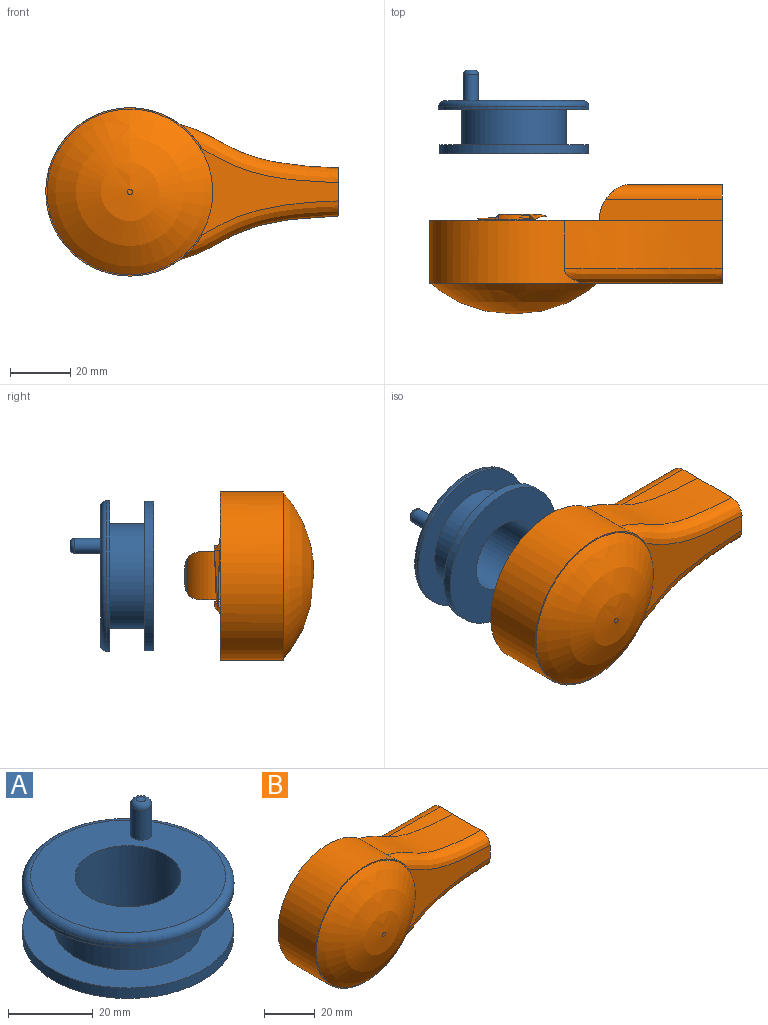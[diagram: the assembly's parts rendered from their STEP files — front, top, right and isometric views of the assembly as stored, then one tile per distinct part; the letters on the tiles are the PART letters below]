
ASSEMBLY  parts=2 mates=1
PART A: 12 faces, bbox 54.1x54.1x27.8 mm
  f0: cylinder r=24.83mm len=49.66mm, axis (0,0,1), area 468.1mm2, adj f1,f6
  f1: plane 49.66x49.66mm, normal (0,0,-1), area 1446.3mm2, adj f0,f8
  f2: plane 46x46mm, normal (0,0,1), area 1151.4mm2, adj f7,f8,f9
  f3: cylinder r=25mm len=50mm, axis (0,0,1), area 157.1mm2, adj f4,f7
  f4: plane 50x50mm, normal (0,0,-1), area 1013.2mm2, adj f3,f5
  f5: cylinder r=17.39mm len=34.78mm, axis (0,0,1), area 1280.1mm2, adj f4,f6
  f6: plane 49.66x49.66mm, normal (0,0,1), area 986.9mm2, adj f0,f5
  f7: torus R=23mm, axis (0,0,1), area 479.1mm2, adj f2,f3
  f8: cylinder r=12.5mm len=25mm, axis (0,0,-1), area 1391.3mm2, adj f1,f2
  f9: cylinder r=2.5mm len=8.65mm, axis (0,0,-1), area 135.9mm2, adj f2,f11
  f10: plane 2.1x2.1mm, normal (0,0,1), area 3.5mm2, adj f11
  f11: torus R=1.05mm, axis (0,0,1), area 28.2mm2, adj f9,f10
PART B: 48 faces, bbox 98.5x43.1x56.2 mm
  f0: plane 31.66x5.98mm, normal (0,1,0), area 189.4mm2, adj f5,f45,f46,f47
  f1: plane 40.96x7mm, normal (0,0,1), area 282mm2, adj f3,f5,f44,f46
  f2: plane 40.96x7mm, normal (0,0,-1), area 282mm2, adj f3,f5,f44,f45
  f3: plane 52.61x44.99mm, normal (0,1,0), area 351.1mm2, adj f1,f2,f6,f8,f9,f44
  f4: plane 97.29x56mm, normal (0,-1,0), area 572.5mm2, adj f5,f6,f10,f11,f16
  f5: plane 32.98x16.16mm, normal (1,0,0), area 393.7mm2, adj f0,f1,f2,f4,f8,f9,f10,f11
  f6: cylinder r=28mm len=56mm, axis (0,-1,0), area 2663.9mm2, adj f3,f4,f7,f8,f9,f10,f11
  f7: plane 56x56mm, normal (0,1,0), area 251.5mm2, adj f6,f17
  f8: extruded ~52.61x15.8mm, area 873.4mm2, adj f3,f5,f6,f11
  f9: extruded ~52.61x15.8mm, area 873.4mm2, adj f3,f5,f6,f10
  f10: bspline ~56.16x19.87mm, area 399.3mm2, adj f4,f5,f6,f9
  f11: bspline ~56.16x19.87mm, area 399.3mm2, adj f4,f5,f6,f8
  f12: cylinder r=1.97mm len=38.53mm, axis (1,0,0), area 472.9mm2, adj f5,f43
  f13: cylinder r=5.55mm len=22mm, axis (1,0,0), area 767.2mm2, adj f5,f14
  f14: plane 11.1x11.1mm, normal (1,0,0), area 96.8mm2, adj f13
  f15: plane 1.77x1.77mm, normal (0,-1,0), area 2.4mm2, adj f16
  f16: torus R=0.88mm, axis (0,1,0), area 2720.3mm2, adj f4,f15
  f17: cylinder r=26.53mm len=53.06mm, axis (0,1,0), area 2871.9mm2, adj f7,f42,f43
  f18: revolved ~13.13x4.04mm, area 38.8mm2, adj f19,f26,f27,f28
  f19: bspline ~14.86x2.84mm, area 3.5mm2, adj f18,f20,f26,f28
  f20: plane 13.07x2.36mm, normal (0,-1,0), area 5.8mm2, adj f19,f26,f28,f29
  f21: revolved ~13.13x4.04mm, area 38.8mm2, adj f22,f30,f31,f32
  f22: bspline ~14.86x2.84mm, area 3.5mm2, adj f21,f23,f30,f32
  f23: plane 13.07x2.36mm, normal (0,-1,0), area 5.8mm2, adj f22,f30,f32,f33
  f24: plane 17.81x5.18mm, normal (0,1,0), area 37.1mm2, adj f34,f35,f36,f37
  f25: plane 17.81x5.18mm, normal (0,1,0), area 37.1mm2, adj f38,f39,f40,f41
  f26: plane 20.02x2.06mm, normal (0.79,0,-0.61), area 39.8mm2, adj f18,f19,f20,f27,f29,f42
  f27: cylinder r=10.03mm len=20mm, axis (0,-1,0), area 220.7mm2, adj f18,f26,f28,f42
  f28: plane 20.02x2.36mm, normal (-0.91,0,-0.42), area 39.8mm2, adj f18,f19,f20,f27,f29,f42
  f29: cylinder r=12.08mm len=18mm, axis (0,-1,0), area 239.1mm2, adj f20,f26,f28,f42
  f30: plane 20.02x2.06mm, normal (-0.79,0,0.61), area 39.8mm2, adj f21,f22,f23,f31,f33,f42
  f31: cylinder r=10.03mm len=20mm, axis (0,-1,0), area 220.7mm2, adj f21,f30,f32,f42
  f32: plane 20.02x2.36mm, normal (0.91,0,0.42), area 39.8mm2, adj f21,f22,f23,f31,f33,f42
  f33: cylinder r=12.08mm len=18mm, axis (0,-1,0), area 239.1mm2, adj f23,f30,f32,f42
  f34: plane 18x1.62mm, normal (0.79,0,0.61), area 37mm2, adj f24,f35,f37,f42
  f35: cylinder r=10.03mm len=18mm, axis (0,-1,0), area 293.5mm2, adj f24,f34,f36,f42
  f36: plane 18x1.62mm, normal (0.79,0,-0.61), area 37mm2, adj f24,f35,f37,f42
  f37: cylinder r=12.08mm len=18mm, axis (0,-1,0), area 360.4mm2, adj f24,f34,f36,f42
  f38: cylinder r=10.03mm len=18mm, axis (0,-1,0), area 293.5mm2, adj f25,f39,f41,f42
  f39: plane 18x1.62mm, normal (-0.79,0,0.61), area 37mm2, adj f25,f38,f40,f42
  f40: cylinder r=12.08mm len=18mm, axis (0,-1,0), area 360.4mm2, adj f25,f39,f41,f42
  f41: plane 18x1.62mm, normal (-0.79,0,-0.61), area 37mm2, adj f25,f38,f40,f42
  f42: plane 53.06x53.06mm, normal (0,1,0), area 2087.5mm2, adj f17,f26,f27,f28,f29,f30,f31,f32
  f43: bspline ~13.96x11.75mm, area 163.8mm2, adj f12,f17
  f44: cylinder r=12.85mm len=15.98mm, axis (0,0,1), area 207.6mm2, adj f1,f2,f3,f45,f46,f47
  f45: cylinder r=5mm len=38.88mm, axis (1,0,0), area 277.4mm2, adj f0,f2,f5,f44,f47
  f46: cylinder r=5mm len=38.88mm, axis (-1,0,0), area 277.4mm2, adj f0,f1,f5,f44,f47
  f47: cylinder r=5mm len=10.52mm, axis (0,0,1), area 19.4mm2, adj f0,f44,f45,f46
PLACE A rot(axis=(0,-0.71,-0.71),180deg) t=(-15.56,-86.87,-0.45)mm
PLACE B rot(axis=(0,1,0),0deg) t=(-15.56,-130.02,-0.45)mm
MATE cylindrical A.f8 <-> B.f17  axis (0,-1,0) through (-15.56,-86.87,-0.45)mm
